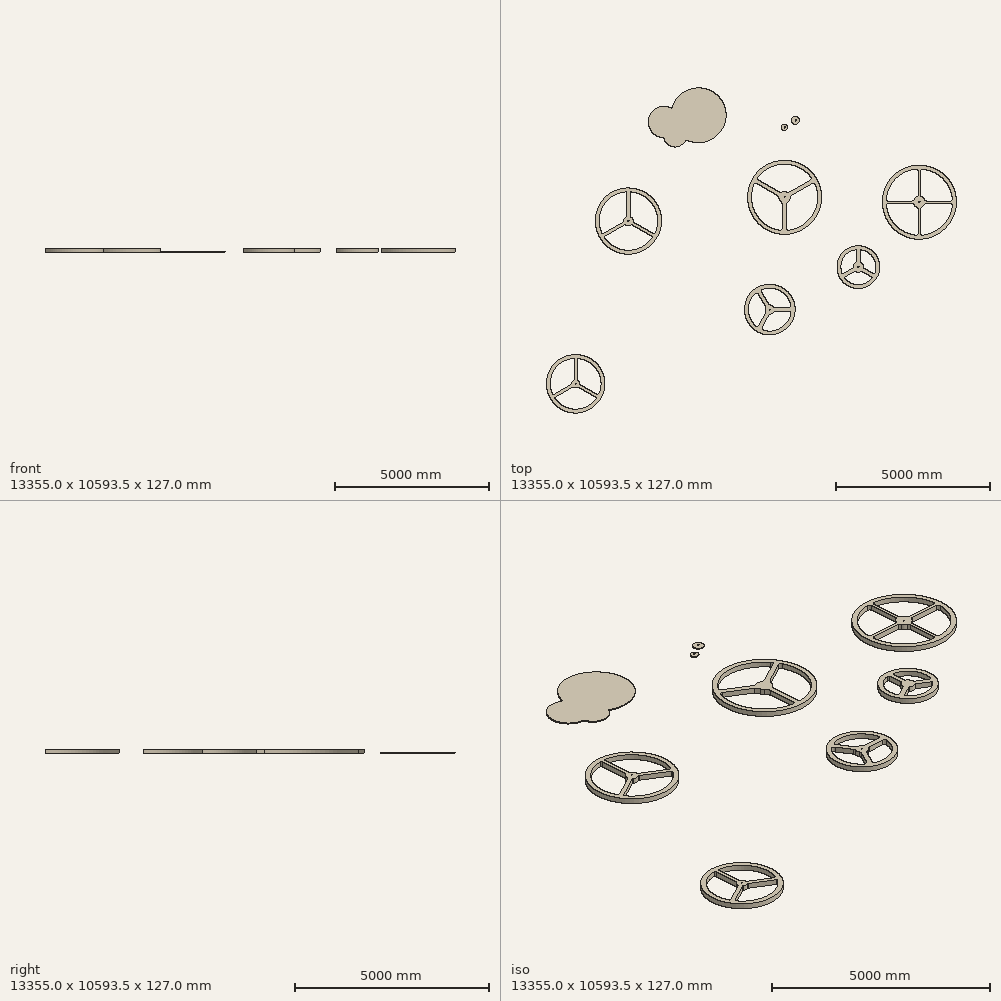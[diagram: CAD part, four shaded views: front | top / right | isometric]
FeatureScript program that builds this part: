
annotation { "Feature Type Name" : "Feature", "Feature Type Description" : "" }
export const myFeature = defineFeature(function(context is Context, id is Id, definition is map)
    precondition{}
    {
        {
            var Q0;
            Q0=qCreatedBy(makeId("Top.planeOp"),FACE);
            var sketch = newSketch(context, id + "F0", { "sketchPlane" : qUnion([Q0])});
            skCircle(sketch, "E0", {"center": v(0, 0) * mm, "radius": 1206.5 * mm});
            skCircle(sketch, "E1", {"center": v(2359.54, 1934.63) * mm, "radius": 304.8 * mm});
            skLineSegment(sketch, "E2", {"start": v(-904.95, 449.15) * mm, "end": v(-250.23, 71.15) * mm});
            skLineSegment(sketch, "E3", {"start": v(-841.45, 559.13) * mm, "end": v(-186.73, 181.13) * mm});
            skArc(sketch, "E4", {"start": v(134.94, -1071.29) * mm, "mid": v(935.1, -539.88) * mm, "end": v(995.23, 418.79) * mm});
            skLineSegment(sketch, "E5.MirrorCS", {"start": v(-63.5, -1008.28) * mm, "end": v(-63.5, -252.28) * mm});
            skLineSegment(sketch, "E6.MirrorCS", {"start": v(63.5, -1008.28) * mm, "end": v(63.5, -252.28) * mm});
            skPoint(sketch, "E7.orphan", {"position": v(-28.72, -56.74) * mm});
            skLineSegment(sketch, "E8.trimOffspring", {"start": v(-935.1, 539.88) * mm, "end": v(-935.78, 540.27) * mm});
            skPoint(sketch, "E9.newPointB", {"position": v(-63.5, -1080.55) * mm});
            skArc(sketch, "E9.filletArc", {"start": v(-134.94, -1071.29) * mm, "mid": v(-85, -1055.9) * mm, "end": v(-63.5, -1008.28) * mm});
            skPoint(sketch, "E10.newPointA", {"position": v(63.5, -1080.55) * mm});
            skArc(sketch, "E10.filletArc", {"start": v(63.5, -1008.28) * mm, "mid": v(85, -1055.9) * mm, "end": v(134.94, -1071.29) * mm});
            skArc(sketch, "E11.MirrorCS", {"start": v(860.3, 652.5) * mm, "mid": v(871.94, 601.56) * mm, "end": v(841.45, 559.13) * mm});
            skArc(sketch, "E12.MirrorCS", {"start": v(904.95, 449.15) * mm, "mid": v(956.94, 454.34) * mm, "end": v(995.23, 418.79) * mm});
            skArc(sketch, "E13.MirrorCS", {"start": v(-860.3, 652.5) * mm, "mid": v(-871.94, 601.56) * mm, "end": v(-841.45, 559.13) * mm});
            skArc(sketch, "E14.MirrorCS", {"start": v(-904.95, 449.15) * mm, "mid": v(-956.94, 454.34) * mm, "end": v(-995.23, 418.79) * mm});
            skArc(sketch, "E15.trimOffspring", {"start": v(-995.23, 418.79) * mm, "mid": v(-935.1, -539.88) * mm, "end": v(-134.94, -1071.29) * mm});
            skLineSegment(sketch, "E16.trimOffspring", {"start": v(841.45, 559.13) * mm, "end": v(186.73, 181.13) * mm});
            skArc(sketch, "E17.trimOffspring", {"start": v(860.3, 652.5) * mm, "mid": v(0, 1079.75) * mm, "end": v(-860.3, 652.5) * mm});
            skLineSegment(sketch, "E18.trimOffspring", {"start": v(904.95, 449.15) * mm, "end": v(250.23, 71.15) * mm});
            skPoint(sketch, "E19.MirrorCS.start.orphan", {"position": v(967.53, 485.28) * mm});
            skPoint(sketch, "E20.MirrorCS.start.orphan", {"position": v(904.03, 595.27) * mm});
            skPoint(sketch, "E21.visualSharp", {"position": v(0, 73.32) * mm});
            skCircle(sketch, "E22", {"center": v(2511.94, 1934.63) * mm, "radius": 80.55 * mm});
            skCircle(sketch, "E23.MirrorC", {"center": v(2359.54, 2087.03) * mm, "radius": 80.55 * mm});
            skCircle(sketch, "E24.MirrorC", {"center": v(2359.54, 1782.23) * mm, "radius": 80.55 * mm});
            skCircle(sketch, "E25.MirrorC", {"center": v(2207.14, 1934.63) * mm, "radius": 80.55 * mm});
            skLineSegment(sketch, "E26.trimOffspring", {"start": v(2431.4, 1934.63) * mm, "end": v(2592.49, 1934.63) * mm});
            skPoint(sketch, "E27.orphan", {"position": v(2664.34, 1934.63) * mm});
            skArc(sketch, "E28", {"start": v(-188.4, -28.18) * mm, "mid": v(-168.26, -89.32) * mm, "end": v(-128.9, -140.26) * mm});
            skLineSegment(sketch, "E29", {"start": v(0, 0) * mm, "end": v(-16.5, 9.53) * mm});
            skArc(sketch, "E30", {"start": v(-186.73, 181.13) * mm, "mid": v(-121.81, 169.22) * mm, "end": v(-57.02, 181.77) * mm});
            skArc(sketch, "E31.MirrorCS", {"start": v(-250.23, 71.15) * mm, "mid": v(-207.46, 20.88) * mm, "end": v(-185.92, -41.5) * mm});
            skLineSegment(sketch, "E32", {"start": v(0, 0) * mm, "end": v(0, -19.05) * mm});
            skArc(sketch, "E33.MirrorCS", {"start": v(186.73, 181.13) * mm, "mid": v(121.81, 169.22) * mm, "end": v(57.02, 181.77) * mm});
            skArc(sketch, "E34.MirrorCS", {"start": v(250.23, 71.15) * mm, "mid": v(207.46, 20.88) * mm, "end": v(185.92, -41.5) * mm});
            skArc(sketch, "E35.MirrorCS", {"start": v(63.5, -252.28) * mm, "mid": v(85.64, -190.1) * mm, "end": v(128.9, -140.26) * mm});
            skArc(sketch, "E36.MirrorCS", {"start": v(-63.5, -252.28) * mm, "mid": v(-85.64, -190.1) * mm, "end": v(-128.9, -140.26) * mm});
            skArc(sketch, "E37.trimOffspring", {"start": v(69.8, 177.25) * mm, "mid": v(0, 190.5) * mm, "end": v(-69.8, 177.25) * mm});
            skArc(sketch, "E38.trimOffspring", {"start": v(118.6, -149.07) * mm, "mid": v(161.49, -101.06) * mm, "end": v(185.92, -41.5) * mm});
            skCircle(sketch, "E39", {"center": v(1177.08, 2703.2) * mm, "radius": 304.8 * mm});
            skCircle(sketch, "E40", {"center": v(1329.48, 2703.2) * mm, "radius": 80.55 * mm});
            skCircle(sketch, "E41.MirrorC", {"center": v(1177.08, 2855.6) * mm, "radius": 80.55 * mm});
            skCircle(sketch, "E42.MirrorC", {"center": v(1177.08, 2550.8) * mm, "radius": 80.55 * mm});
            skCircle(sketch, "E43.MirrorC", {"center": v(1024.68, 2703.2) * mm, "radius": 80.55 * mm});
            skLineSegment(sketch, "E44.trimOffspring", {"start": v(1248.93, 2703.2) * mm, "end": v(1410.03, 2703.2) * mm});
            skPoint(sketch, "E45.orphan", {"position": v(1481.88, 2703.2) * mm});
            skCircle(sketch, "E46", {"center": v(1177.08, 2703.2) * mm, "radius": 21.59 * mm});
            skLineSegment(sketch, "E47", {"start": v(1177.08, 2703.2) * mm, "end": v(1177.08, 2724.8) * mm});
            skLineSegment(sketch, "E48", {"start": v(1177.08, 2703.2) * mm, "end": v(1192.35, 2718.47) * mm});
            skLineSegment(sketch, "E49", {"start": v(1177.08, 2855.6) * mm, "end": v(1177.08, 2936.15) * mm});
            skLineSegment(sketch, "E50", {"start": v(1177.08, 2703.2) * mm, "end": v(1198.67, 2703.2) * mm});
            skLineSegment(sketch, "E51", {"start": v(1296.75, 2822.88) * mm, "end": v(1367.02, 2893.15) * mm});
            skCircle(sketch, "E52", {"center": v(1331.89, 2858.01) * mm, "radius": 49.69 * mm});
            skCircle(sketch, "E53.MirrorC", {"center": v(1022.27, 2858.01) * mm, "radius": 49.69 * mm});
            skCircle(sketch, "E54.MirrorC", {"center": v(1022.27, 2548.4) * mm, "radius": 49.69 * mm});
            skCircle(sketch, "E55.MirrorC", {"center": v(1331.89, 2548.4) * mm, "radius": 49.69 * mm});
            skLineSegment(sketch, "E56.trimOffspring", {"start": v(1177.08, 2775.06) * mm, "end": v(1177.08, 2855.6) * mm});
            skCircle(sketch, "E57", {"center": v(4388.83, -157.21) * mm, "radius": 1206.5 * mm});
            skCircle(sketch, "E58", {"center": v(4388.83, -157.21) * mm, "radius": 22.86 * mm});
            skArc(sketch, "E59", {"start": v(4465.03, -331.81) * mm, "mid": v(4523.53, -291.92) * mm, "end": v(4563.43, -233.41) * mm});
            skArc(sketch, "E60", {"start": v(4496.78, -1231.3) * mm, "mid": v(5152.15, -920.54) * mm, "end": v(5462.92, -265.16) * mm});
            skLineSegment(sketch, "E61", {"start": v(4388.83, -157.21) * mm, "end": v(4388.83, -180.07) * mm});
            skLineSegment(sketch, "E62", {"start": v(4388.83, -157.21) * mm, "end": v(4405, -173.38) * mm});
            skLineSegment(sketch, "E63.bottom", {"start": v(6717.68, -259.59) * mm, "end": v(7126.18, -259.59) * mm});
            skLineSegment(sketch, "E63.top", {"start": v(6781.18, -1038.61) * mm, "end": v(7126.18, -1038.61) * mm});
            skLineSegment(sketch, "E63.left", {"start": v(6717.68, -259.59) * mm, "end": v(6717.68, -975.11) * mm});
            skLineSegment(sketch, "E63.right", {"start": v(7189.68, -323.09) * mm, "end": v(7189.68, -975.11) * mm});
            skPoint(sketch, "E64.visualSharp", {"position": v(7189.68, -259.59) * mm});
            skArc(sketch, "E64.filletArc", {"start": v(7189.68, -323.09) * mm, "mid": v(7171.08, -278.19) * mm, "end": v(7126.18, -259.59) * mm});
            skPoint(sketch, "E65.visualSharp", {"position": v(6717.68, -1038.61) * mm});
            skArc(sketch, "E65.filletArc", {"start": v(6717.68, -975.11) * mm, "mid": v(6736.28, -1020.02) * mm, "end": v(6781.18, -1038.61) * mm});
            skPoint(sketch, "E66.visualSharp", {"position": v(4426.93, -343.87) * mm});
            skArc(sketch, "E66.filletArc", {"start": v(4465.03, -331.81) * mm, "mid": v(4437.3, -355.23) * mm, "end": v(4426.93, -390) * mm});
            skPoint(sketch, "E67.visualSharp", {"position": v(4350.73, -343.87) * mm});
            skArc(sketch, "E67.filletArc", {"start": v(4350.73, -390) * mm, "mid": v(4340.36, -355.23) * mm, "end": v(4312.63, -331.81) * mm});
            skLineSegment(sketch, "E68", {"start": v(4350.73, -1168.12) * mm, "end": v(4350.73, -390) * mm});
            skLineSegment(sketch, "E69", {"start": v(4426.93, -390) * mm, "end": v(4426.93, -1168.12) * mm});
            skPoint(sketch, "E70.visualSharp", {"position": v(7189.68, -1038.61) * mm});
            skArc(sketch, "E70.filletArc", {"start": v(7126.18, -1038.61) * mm, "mid": v(7171.08, -1020.02) * mm, "end": v(7189.68, -975.11) * mm});
            skPoint(sketch, "E71.visualSharp", {"position": v(4426.93, -1236.04) * mm});
            skArc(sketch, "E71.filletArc", {"start": v(4426.93, -1168.12) * mm, "mid": v(4447.83, -1215.21) * mm, "end": v(4496.78, -1231.3) * mm});
            skPoint(sketch, "E72.visualSharp", {"position": v(4350.73, -1236.04) * mm});
            skArc(sketch, "E72.filletArc", {"start": v(4280.88, -1231.3) * mm, "mid": v(4329.83, -1215.21) * mm, "end": v(4350.73, -1168.12) * mm});
            skArc(sketch, "E73.MirrorCS", {"start": v(4563.43, -233.41) * mm, "mid": v(4586.85, -205.69) * mm, "end": v(4621.63, -195.31) * mm});
            skArc(sketch, "E74.MirrorCS", {"start": v(4621.63, -119.11) * mm, "mid": v(4586.85, -108.74) * mm, "end": v(4563.43, -81.01) * mm});
            skLineSegment(sketch, "E75.MirrorCS", {"start": v(5399.74, -119.11) * mm, "end": v(4621.63, -119.11) * mm});
            skLineSegment(sketch, "E76.MirrorCS", {"start": v(4621.63, -195.31) * mm, "end": v(5399.74, -195.31) * mm});
            skArc(sketch, "E77.MirrorCS", {"start": v(5399.74, -195.31) * mm, "mid": v(5446.83, -216.22) * mm, "end": v(5462.92, -265.16) * mm});
            skArc(sketch, "E78.MirrorCS", {"start": v(5462.92, -49.26) * mm, "mid": v(5446.83, -98.21) * mm, "end": v(5399.74, -119.11) * mm});
            skArc(sketch, "E79.MirrorCS", {"start": v(4156.04, -119.11) * mm, "mid": v(4190.82, -108.74) * mm, "end": v(4214.23, -81.01) * mm});
            skLineSegment(sketch, "E80.MirrorCS", {"start": v(3377.92, -119.11) * mm, "end": v(4156.04, -119.11) * mm});
            skLineSegment(sketch, "E81.MirrorCS", {"start": v(4156.04, -195.31) * mm, "end": v(3377.92, -195.31) * mm});
            skArc(sketch, "E82.MirrorCS", {"start": v(4214.23, -233.41) * mm, "mid": v(4190.82, -205.69) * mm, "end": v(4156.04, -195.31) * mm});
            skArc(sketch, "E83.MirrorCS", {"start": v(3377.92, -195.31) * mm, "mid": v(3330.83, -216.22) * mm, "end": v(3314.74, -265.16) * mm});
            skArc(sketch, "E84.MirrorCS", {"start": v(3314.74, -49.26) * mm, "mid": v(3330.83, -98.21) * mm, "end": v(3377.92, -119.11) * mm});
            skLineSegment(sketch, "E85.MirrorCS", {"start": v(4426.93, 75.58) * mm, "end": v(4426.93, 853.7) * mm});
            skLineSegment(sketch, "E86.MirrorCS", {"start": v(4350.73, 853.7) * mm, "end": v(4350.73, 75.58) * mm});
            skArc(sketch, "E87.MirrorCS", {"start": v(4350.73, 75.58) * mm, "mid": v(4340.36, 40.8) * mm, "end": v(4312.63, 17.38) * mm});
            skPoint(sketch, "E88.MirrorP", {"position": v(4426.93, 29.44) * mm});
            skArc(sketch, "E89.MirrorCS", {"start": v(4465.03, 17.38) * mm, "mid": v(4437.3, 40.8) * mm, "end": v(4426.93, 75.58) * mm});
            skArc(sketch, "E90.MirrorCS", {"start": v(4426.93, 853.7) * mm, "mid": v(4447.83, 900.79) * mm, "end": v(4496.78, 916.87) * mm});
            skArc(sketch, "E91.MirrorCS", {"start": v(4280.88, 916.87) * mm, "mid": v(4329.83, 900.79) * mm, "end": v(4350.73, 853.7) * mm});
            skArc(sketch, "E92.trimOffspring", {"start": v(3314.74, -265.16) * mm, "mid": v(3625.5, -920.54) * mm, "end": v(4280.88, -1231.3) * mm});
            skArc(sketch, "E93.trimOffspring", {"start": v(4214.23, -233.41) * mm, "mid": v(4254.13, -291.92) * mm, "end": v(4312.63, -331.81) * mm});
            skArc(sketch, "E94.trimOffspring", {"start": v(4312.63, 17.38) * mm, "mid": v(4254.13, -22.51) * mm, "end": v(4214.23, -81.01) * mm});
            skArc(sketch, "E95.trimOffspring", {"start": v(4563.43, -81.01) * mm, "mid": v(4523.53, -22.51) * mm, "end": v(4465.03, 17.38) * mm});
            skLineSegment(sketch, "E96.trimOffspring", {"start": v(4523.53, -291.92) * mm, "end": v(5152.15, -920.54) * mm});
            skArc(sketch, "E97.trimOffspring", {"start": v(5462.92, -49.26) * mm, "mid": v(5152.15, 606.1) * mm, "end": v(4496.78, 916.87) * mm});
            skArc(sketch, "E98.trimOffspring", {"start": v(4280.88, 916.87) * mm, "mid": v(3625.5, 606.1) * mm, "end": v(3314.74, -49.26) * mm});
            skCircle(sketch, "E99", {"center": v(2359.54, 1934.63) * mm, "radius": 20.32 * mm});
            skCircle(sketch, "E100", {"center": v(0, 2278.33) * mm, "radius": 22.99 * mm});
            skCircle(sketch, "E101", {"center": v(0, 0) * mm, "radius": 19.05 * mm});
            skCircle(sketch, "E102", {"center": v(2402.2, -2273.62) * mm, "radius": 698.5 * mm});
            skArc(sketch, "E103", {"start": v(2309.16, -1709.75) * mm, "mid": v(1907.27, -1987.87) * mm, "end": v(1867.35, -2475) * mm});
            skArc(sketch, "E104", {"start": v(2325.15, -2127.6) * mm, "mid": v(2259.22, -2191.07) * mm, "end": v(2237.22, -2279.9) * mm});
            skLineSegment(sketch, "E105", {"start": v(2338.7, -1769.9) * mm, "end": v(2338.7, -2105.14) * mm});
            skLineSegment(sketch, "E106", {"start": v(2465.7, -1769.9) * mm, "end": v(2465.7, -2121.22) * mm});
            skLineSegment(sketch, "E107", {"start": v(2465.7, -2105.14) * mm, "end": v(2465.7, -1734.8) * mm});
            skLineSegment(sketch, "E108", {"start": v(2338.7, -1769.9) * mm, "end": v(2338.7, -1734.8) * mm});
            skLineSegment(sketch, "E109", {"start": v(1999.56, -1360.97) * mm, "end": v(1999.56, -1432.2) * mm});
            skLineSegment(sketch, "E110", {"start": v(2024.96, -1457.6) * mm, "end": v(2120.48, -1457.6) * mm});
            skPoint(sketch, "E111.visualSharp", {"position": v(1999.56, -1457.6) * mm});
            skArc(sketch, "E111.filletArc", {"start": v(1999.56, -1432.2) * mm, "mid": v(2007, -1450.16) * mm, "end": v(2024.96, -1457.6) * mm});
            skPoint(sketch, "E112.visualSharp", {"position": v(2338.7, -1705.66) * mm});
            skArc(sketch, "E112.filletArc", {"start": v(2338.7, -1734.8) * mm, "mid": v(2329.73, -1715.44) * mm, "end": v(2309.16, -1709.75) * mm});
            skPoint(sketch, "E113.visualSharp", {"position": v(2465.7, -1705.66) * mm});
            skArc(sketch, "E113.filletArc", {"start": v(2495.23, -1709.75) * mm, "mid": v(2474.66, -1715.44) * mm, "end": v(2465.7, -1734.8) * mm});
            skPoint(sketch, "E114.visualSharp", {"position": v(2338.7, -2121.22) * mm});
            skArc(sketch, "E114.filletArc", {"start": v(2325.15, -2127.6) * mm, "mid": v(2335.05, -2118.26) * mm, "end": v(2338.7, -2105.14) * mm});
            skPoint(sketch, "E115.visualSharp", {"position": v(2465.7, -2121.22) * mm});
            skArc(sketch, "E115.filletArc", {"start": v(2465.7, -2105.14) * mm, "mid": v(2469.35, -2118.26) * mm, "end": v(2479.25, -2127.6) * mm});
            skLineSegment(sketch, "E116.MirrorCS", {"start": v(1934.21, -2470.5) * mm, "end": v(2224.54, -2302.87) * mm});
            skLineSegment(sketch, "E117.MirrorCS", {"start": v(2288.04, -2412.86) * mm, "end": v(1967.32, -2598.02) * mm});
            skArc(sketch, "E118.MirrorCS", {"start": v(2237.22, -2279.9) * mm, "mid": v(2234.07, -2293.16) * mm, "end": v(2224.54, -2302.87) * mm});
            skArc(sketch, "E119.MirrorCS", {"start": v(2288.04, -2412.86) * mm, "mid": v(2301.22, -2409.46) * mm, "end": v(2314.26, -2413.36) * mm});
            skArc(sketch, "E120.MirrorCS", {"start": v(1903.82, -2488.04) * mm, "mid": v(1882.57, -2489.96) * mm, "end": v(1867.35, -2475) * mm});
            skArc(sketch, "E121.MirrorCS", {"start": v(1960.38, -2636.13) * mm, "mid": v(1955.03, -2615.47) * mm, "end": v(1967.32, -2598.02) * mm});
            skLineSegment(sketch, "E122.MirrorCS", {"start": v(1934.21, -2470.5) * mm, "end": v(1903.82, -2488.04) * mm});
            skLineSegment(sketch, "E123.MirrorCS", {"start": v(2870.19, -2470.5) * mm, "end": v(2579.86, -2302.87) * mm});
            skLineSegment(sketch, "E124.MirrorCS", {"start": v(2516.36, -2412.86) * mm, "end": v(2837.08, -2598.02) * mm});
            skArc(sketch, "E125.MirrorCS", {"start": v(2516.36, -2412.86) * mm, "mid": v(2503.18, -2409.46) * mm, "end": v(2490.13, -2413.36) * mm});
            skArc(sketch, "E126.MirrorCS", {"start": v(2479.25, -2127.6) * mm, "mid": v(2545.18, -2191.07) * mm, "end": v(2567.18, -2279.9) * mm});
            skArc(sketch, "E127.MirrorCS", {"start": v(2567.18, -2279.9) * mm, "mid": v(2570.33, -2293.16) * mm, "end": v(2579.86, -2302.87) * mm});
            skArc(sketch, "E128.MirrorCS", {"start": v(2900.58, -2488.04) * mm, "mid": v(2921.83, -2489.96) * mm, "end": v(2937.05, -2475) * mm});
            skArc(sketch, "E129.MirrorCS", {"start": v(2844.01, -2636.13) * mm, "mid": v(2849.37, -2615.47) * mm, "end": v(2837.08, -2598.02) * mm});
            skLineSegment(sketch, "E130.MirrorCS", {"start": v(2870.19, -2470.5) * mm, "end": v(2900.58, -2488.04) * mm});
            skArc(sketch, "E131.trimOffspring", {"start": v(1960.38, -2636.13) * mm, "mid": v(2402.2, -2845.12) * mm, "end": v(2844.01, -2636.13) * mm});
            skArc(sketch, "E132.trimOffspring", {"start": v(2937.05, -2475) * mm, "mid": v(2897.13, -1987.87) * mm, "end": v(2495.23, -1709.75) * mm});
            skArc(sketch, "E133.trimOffspring", {"start": v(2567.18, -2279.9) * mm, "mid": v(2545.18, -2191.07) * mm, "end": v(2479.25, -2127.6) * mm});
            skArc(sketch, "E134.trimOffspring", {"start": v(2314.26, -2413.36) * mm, "mid": v(2402.2, -2438.72) * mm, "end": v(2490.13, -2413.36) * mm});
            skArc(sketch, "E135.trimOffspring", {"start": v(2490.13, -2413.36) * mm, "mid": v(2402.2, -2438.72) * mm, "end": v(2314.26, -2413.36) * mm});
            skArc(sketch, "E136.trimOffspring", {"start": v(2237.22, -2279.9) * mm, "mid": v(2259.22, -2191.07) * mm, "end": v(2325.15, -2127.6) * mm});
            skCircle(sketch, "E137", {"center": v(2402.2, -2273.62) * mm, "radius": 19.05 * mm});
            skCircle(sketch, "E138", {"center": v(-482.79, -3656.25) * mm, "radius": 825.5 * mm});
            skArc(sketch, "E139", {"start": v(-623.21, -3597.03) * mm, "mid": v(-635.16, -3659.18) * mm, "end": v(-620.83, -3720.83) * mm});
            skLineSegment(sketch, "E140", {"start": v(-518.6, -3473.95) * mm, "end": v(-749.8, -3090.72) * mm});
            skLineSegment(sketch, "E141", {"start": v(-749.8, -3090.72) * mm, "end": v(-518.6, -3473.95) * mm});
            skPoint(sketch, "E142.visualSharp", {"position": v(-787.74, -3027.83) * mm});
            skArc(sketch, "E142.filletArc", {"start": v(-716.7, -2998.08) * mm, "mid": v(-755.23, -3036.54) * mm, "end": v(-749.8, -3090.72) * mm});
            skPoint(sketch, "E143.visualSharp", {"position": v(-499.98, -3504.82) * mm});
            skArc(sketch, "E143.filletArc", {"start": v(-518.6, -3473.95) * mm, "mid": v(-497.8, -3495.05) * mm, "end": v(-469.7, -3504.42) * mm});
            skArc(sketch, "E144.MirrorCS", {"start": v(-955.93, -3142.4) * mm, "mid": v(-903.94, -3126.26) * mm, "end": v(-858.55, -3156.32) * mm});
            skLineSegment(sketch, "E145.MirrorCS", {"start": v(-627.35, -3539.55) * mm, "end": v(-858.55, -3156.32) * mm});
            skArc(sketch, "E146.MirrorCS", {"start": v(-627.35, -3539.55) * mm, "mid": v(-618.38, -3567.8) * mm, "end": v(-623.21, -3597.03) * mm});
            skPoint(sketch, "E147.orphan", {"position": v(-896.48, -3093.44) * mm});
            skArc(sketch, "E148.trimOffspring", {"start": v(-955.93, -3142.4) * mm, "mid": v(-1181.16, -3669.68) * mm, "end": v(-935.83, -4187.9) * mm});
            skPoint(sketch, "E149.orphan", {"position": v(-507.14, -3492.96) * mm});
            skPoint(sketch, "E150.orphan", {"position": v(-615.88, -3558.56) * mm});
            skLineSegment(sketch, "E151.MirrorCS", {"start": v(-307, -3716.38) * mm, "end": v(140.49, -3707.78) * mm});
            skLineSegment(sketch, "E152.MirrorCS", {"start": v(138.05, -3580.8) * mm, "end": v(-309.44, -3589.4) * mm});
            skArc(sketch, "E153.MirrorCS", {"start": v(-309.44, -3589.4) * mm, "mid": v(-338.38, -3583.05) * mm, "end": v(-361.29, -3564.25) * mm});
            skArc(sketch, "E154.MirrorCS", {"start": v(-307, -3716.38) * mm, "mid": v(-335.68, -3723.85) * mm, "end": v(-357.84, -3743.51) * mm});
            skArc(sketch, "E155.MirrorCS", {"start": v(204.16, -3782.77) * mm, "mid": v(190.12, -3730.17) * mm, "end": v(140.49, -3707.78) * mm});
            skArc(sketch, "E156.MirrorCS", {"start": v(198.79, -3503.42) * mm, "mid": v(186.78, -3556.52) * mm, "end": v(138.05, -3580.8) * mm});
            skLineSegment(sketch, "E157.MirrorCS", {"start": v(-622.76, -3778.42) * mm, "end": v(-839.05, -4170.26) * mm});
            skLineSegment(sketch, "E158.MirrorCS", {"start": v(-727.86, -4231.63) * mm, "end": v(-511.57, -3839.8) * mm});
            skArc(sketch, "E159.MirrorCS", {"start": v(-691.22, -4322.93) * mm, "mid": v(-731.2, -4285.98) * mm, "end": v(-727.86, -4231.63) * mm});
            skArc(sketch, "E160.MirrorCS", {"start": v(-935.83, -4187.9) * mm, "mid": v(-883.25, -4202.04) * mm, "end": v(-839.05, -4170.26) * mm});
            skArc(sketch, "E161.MirrorCS", {"start": v(-511.57, -3839.8) * mm, "mid": v(-491.6, -3817.9) * mm, "end": v(-463.86, -3807.47) * mm});
            skArc(sketch, "E162.MirrorCS", {"start": v(-622.76, -3778.42) * mm, "mid": v(-614.88, -3749.85) * mm, "end": v(-620.83, -3720.83) * mm});
            skArc(sketch, "E163.trimOffspring", {"start": v(-463.86, -3807.47) * mm, "mid": v(-404.06, -3786.74) * mm, "end": v(-357.84, -3743.51) * mm});
            skArc(sketch, "E164.trimOffspring", {"start": v(-361.29, -3564.25) * mm, "mid": v(-409.14, -3522.83) * mm, "end": v(-469.7, -3504.42) * mm});
            skArc(sketch, "E165.trimOffspring", {"start": v(198.79, -3503.42) * mm, "mid": v(-145.23, -3044.73) * mm, "end": v(-716.7, -2998.08) * mm});
            skArc(sketch, "E166.trimOffspring", {"start": v(-691.22, -4322.93) * mm, "mid": v(-121.97, -4254.34) * mm, "end": v(204.16, -3782.77) * mm});
            skCircle(sketch, "E167", {"center": v(-482.79, -3656.25) * mm, "radius": 19.05 * mm});
            skCircle(sketch, "E168", {"center": v(-5086.57, -770.76) * mm, "radius": 1079.5 * mm});
            skArc(sketch, "E169", {"start": v(-5164.86, 178.51) * mm, "mid": v(-5911.46, -294.51) * mm, "end": v(-5947.81, -1177.6) * mm});
            skArc(sketch, "E170", {"start": v(-5151.88, -633.07) * mm, "mid": v(-5218.55, -694.56) * mm, "end": v(-5238.47, -783.05) * mm});
            skCircle(sketch, "E171", {"center": v(0, 2278.33) * mm, "radius": 101.6 * mm});
            skCircle(sketch, "E172", {"center": v(355.23, 2506.68) * mm, "radius": 22.99 * mm});
            skCircle(sketch, "E173", {"center": v(355.23, 2506.68) * mm, "radius": 134.38 * mm});
            skCircle(sketch, "E174", {"center": v(-6807.19, -6073.12) * mm, "radius": 952.5 * mm});
            skArc(sketch, "E175", {"start": v(-6885.8, -5251.38) * mm, "mid": v(-7522.1, -5660.37) * mm, "end": v(-7558.15, -6415.91) * mm});
            skLineSegment(sketch, "E176", {"start": v(-5137.37, 153.2) * mm, "end": v(-5137.37, -610.12) * mm});
            skLineSegment(sketch, "E177", {"start": v(-5035.77, 153.2) * mm, "end": v(-5035.77, -610.12) * mm});
            skLineSegment(sketch, "E178.bottom", {"start": v(-3589.34, -293.86) * mm, "end": v(-3407.23, -293.86) * mm});
            skLineSegment(sketch, "E178.top", {"start": v(-3570.29, -575.44) * mm, "end": v(-3419.93, -575.44) * mm});
            skLineSegment(sketch, "E178.left", {"start": v(-3595.69, -300.21) * mm, "end": v(-3595.69, -550.04) * mm});
            skLineSegment(sketch, "E178.right", {"start": v(-3394.53, -306.56) * mm, "end": v(-3394.53, -550.04) * mm});
            skPoint(sketch, "E179.visualSharp", {"position": v(-3595.69, -293.86) * mm});
            skArc(sketch, "E179.filletArc", {"start": v(-3589.34, -293.86) * mm, "mid": v(-3593.83, -295.72) * mm, "end": v(-3595.69, -300.21) * mm});
            skPoint(sketch, "E180.visualSharp", {"position": v(-3394.53, -293.86) * mm});
            skArc(sketch, "E180.filletArc", {"start": v(-3394.53, -306.56) * mm, "mid": v(-3398.25, -297.58) * mm, "end": v(-3407.23, -293.86) * mm});
            skPoint(sketch, "E181.visualSharp", {"position": v(-3394.53, -575.44) * mm});
            skArc(sketch, "E181.filletArc", {"start": v(-3419.93, -575.44) * mm, "mid": v(-3401.97, -568) * mm, "end": v(-3394.53, -550.04) * mm});
            skPoint(sketch, "E182.visualSharp", {"position": v(-3595.69, -575.44) * mm});
            skArc(sketch, "E182.filletArc", {"start": v(-3595.69, -550.04) * mm, "mid": v(-3588.25, -568) * mm, "end": v(-3570.29, -575.44) * mm});
            skPoint(sketch, "E183.visualSharp", {"position": v(-5035.77, 180.38) * mm});
            skArc(sketch, "E183.filletArc", {"start": v(-5008.28, 178.51) * mm, "mid": v(-5027.58, 171.88) * mm, "end": v(-5035.77, 153.2) * mm});
            skPoint(sketch, "E184.visualSharp", {"position": v(-5137.37, 180.38) * mm});
            skArc(sketch, "E184.filletArc", {"start": v(-5137.37, 153.2) * mm, "mid": v(-5145.56, 171.88) * mm, "end": v(-5164.86, 178.51) * mm});
            skLineSegment(sketch, "E185.bottom", {"start": v(-3521.85, 165.33) * mm, "end": v(-3268.73, 165.33) * mm});
            skLineSegment(sketch, "E185.top", {"start": v(-3496.45, -14.92) * mm, "end": v(-3268.73, -14.92) * mm});
            skLineSegment(sketch, "E185.left", {"start": v(-3521.85, 165.33) * mm, "end": v(-3521.85, 10.48) * mm});
            skLineSegment(sketch, "E185.right", {"start": v(-3268.73, 165.33) * mm, "end": v(-3268.73, -14.92) * mm});
            skPoint(sketch, "E186.visualSharp", {"position": v(-3521.85, -14.92) * mm});
            skArc(sketch, "E186.filletArc", {"start": v(-3521.85, 10.48) * mm, "mid": v(-3514.41, -7.48) * mm, "end": v(-3496.45, -14.92) * mm});
            skPoint(sketch, "E187.visualSharp", {"position": v(-5035.77, -627.08) * mm});
            skArc(sketch, "E187.filletArc", {"start": v(-5035.77, -610.12) * mm, "mid": v(-5031.84, -623.7) * mm, "end": v(-5021.26, -633.07) * mm});
            skPoint(sketch, "E188.visualSharp", {"position": v(-5137.37, -627.08) * mm});
            skArc(sketch, "E188.filletArc", {"start": v(-5151.88, -633.07) * mm, "mid": v(-5141.3, -623.7) * mm, "end": v(-5137.37, -610.12) * mm});
            skLineSegment(sketch, "E189.MirrorCS", {"start": v(-5861.35, -1276.74) * mm, "end": v(-5200.3, -895.08) * mm});
            skLineSegment(sketch, "E190.MirrorCS", {"start": v(-5912.15, -1188.75) * mm, "end": v(-5251.1, -807.1) * mm});
            skArc(sketch, "E191.MirrorCS", {"start": v(-5238.47, -783.05) * mm, "mid": v(-5241.3, -796.9) * mm, "end": v(-5251.1, -807.1) * mm});
            skArc(sketch, "E192.MirrorCS", {"start": v(-5200.3, -895.08) * mm, "mid": v(-5186.57, -891.7) * mm, "end": v(-5173.16, -896.17) * mm});
            skArc(sketch, "E193.MirrorCS", {"start": v(-5912.15, -1188.75) * mm, "mid": v(-5932.42, -1191) * mm, "end": v(-5947.81, -1177.6) * mm});
            skArc(sketch, "E194.MirrorCS", {"start": v(-5869.52, -1313.2) * mm, "mid": v(-5873.43, -1293.18) * mm, "end": v(-5861.35, -1276.74) * mm});
            skLineSegment(sketch, "E195.MirrorCS", {"start": v(-4261, -1188.75) * mm, "end": v(-4922.05, -807.1) * mm});
            skLineSegment(sketch, "E196.MirrorCS", {"start": v(-4311.8, -1276.74) * mm, "end": v(-4972.85, -895.08) * mm});
            skArc(sketch, "E197.MirrorCS", {"start": v(-4999.98, -896.17) * mm, "mid": v(-4986.57, -891.7) * mm, "end": v(-4972.85, -895.08) * mm});
            skArc(sketch, "E198.MirrorCS", {"start": v(-4922.05, -807.1) * mm, "mid": v(-4931.84, -796.9) * mm, "end": v(-4934.67, -783.05) * mm});
            skArc(sketch, "E199.MirrorCS", {"start": v(-4311.8, -1276.74) * mm, "mid": v(-4299.71, -1293.18) * mm, "end": v(-4303.62, -1313.2) * mm});
            skArc(sketch, "E200.MirrorCS", {"start": v(-4225.33, -1177.6) * mm, "mid": v(-4240.72, -1191) * mm, "end": v(-4261, -1188.75) * mm});
            skArc(sketch, "E201.trimOffspring", {"start": v(-5869.52, -1313.2) * mm, "mid": v(-5086.57, -1723.26) * mm, "end": v(-4303.62, -1313.2) * mm});
            skArc(sketch, "E202.trimOffspring", {"start": v(-4225.33, -1177.6) * mm, "mid": v(-4261.68, -294.51) * mm, "end": v(-5008.28, 178.51) * mm});
            skArc(sketch, "E203.trimOffspring", {"start": v(-4934.67, -783.05) * mm, "mid": v(-4954.59, -694.56) * mm, "end": v(-5021.26, -633.07) * mm});
            skArc(sketch, "E204.trimOffspring", {"start": v(-5173.16, -896.17) * mm, "mid": v(-5086.57, -923.16) * mm, "end": v(-4999.98, -896.17) * mm});
            skArc(sketch, "E205", {"start": v(-6870.69, -5963.14) * mm, "mid": v(-6917.18, -6009.62) * mm, "end": v(-6934.19, -6073.12) * mm});
            skLineSegment(sketch, "E206", {"start": v(-6756.39, -5276.66) * mm, "end": v(-6756.39, -5941.14) * mm});
            skLineSegment(sketch, "E207", {"start": v(-6857.99, -5276.66) * mm, "end": v(-6857.99, -5941.14) * mm});
            skLineSegment(sketch, "E208.bottom", {"start": v(-8632.4, -5662.84) * mm, "end": v(-8538.47, -5662.84) * mm});
            skLineSegment(sketch, "E208.top", {"start": v(-8632.4, -5862.78) * mm, "end": v(-8513.07, -5862.78) * mm});
            skLineSegment(sketch, "E208.left", {"start": v(-8632.4, -5662.84) * mm, "end": v(-8632.4, -5862.78) * mm});
            skLineSegment(sketch, "E208.right", {"start": v(-8513.07, -5688.24) * mm, "end": v(-8513.07, -5862.78) * mm});
            skPoint(sketch, "E209.visualSharp", {"position": v(-8513.07, -5662.84) * mm});
            skArc(sketch, "E209.filletArc", {"start": v(-8513.07, -5688.24) * mm, "mid": v(-8520.51, -5670.28) * mm, "end": v(-8538.47, -5662.84) * mm});
            skPoint(sketch, "E210.visualSharp", {"position": v(-6756.39, -5249.19) * mm});
            skArc(sketch, "E210.filletArc", {"start": v(-6728.57, -5251.38) * mm, "mid": v(-6748.07, -5257.86) * mm, "end": v(-6756.39, -5276.66) * mm});
            skPoint(sketch, "E211.visualSharp", {"position": v(-6857.99, -5249.19) * mm});
            skArc(sketch, "E211.filletArc", {"start": v(-6857.99, -5276.66) * mm, "mid": v(-6866.3, -5257.86) * mm, "end": v(-6885.8, -5251.38) * mm});
            skPoint(sketch, "E212.visualSharp", {"position": v(-6756.39, -5956.73) * mm});
            skArc(sketch, "E212.filletArc", {"start": v(-6756.39, -5941.14) * mm, "mid": v(-6752.99, -5953.84) * mm, "end": v(-6743.69, -5963.14) * mm});
            skPoint(sketch, "E213.visualSharp", {"position": v(-6857.99, -5956.73) * mm});
            skArc(sketch, "E213.filletArc", {"start": v(-6870.69, -5963.14) * mm, "mid": v(-6861.4, -5953.84) * mm, "end": v(-6857.99, -5941.14) * mm});
            skArc(sketch, "E214.MirrorCS", {"start": v(-6743.69, -6183.1) * mm, "mid": v(-6730.99, -6179.7) * mm, "end": v(-6718.29, -6183.1) * mm});
            skLineSegment(sketch, "E215.MirrorCS", {"start": v(-6142.83, -6515.35) * mm, "end": v(-6718.29, -6183.1) * mm});
            skArc(sketch, "E216.MirrorCS", {"start": v(-6667.49, -6095.12) * mm, "mid": v(-6676.79, -6085.82) * mm, "end": v(-6680.19, -6073.12) * mm});
            skLineSegment(sketch, "E217.MirrorCS", {"start": v(-6092.03, -6427.36) * mm, "end": v(-6667.49, -6095.12) * mm});
            skArc(sketch, "E218.MirrorCS", {"start": v(-6142.83, -6515.35) * mm, "mid": v(-6130.71, -6531.95) * mm, "end": v(-6134.84, -6552.08) * mm});
            skArc(sketch, "E219.MirrorCS", {"start": v(-6056.23, -6415.91) * mm, "mid": v(-6071.6, -6429.56) * mm, "end": v(-6092.03, -6427.36) * mm});
            skLineSegment(sketch, "E220.MirrorCS", {"start": v(-7471.55, -6515.35) * mm, "end": v(-6896.09, -6183.1) * mm});
            skLineSegment(sketch, "E221.MirrorCS", {"start": v(-7522.35, -6427.36) * mm, "end": v(-6946.89, -6095.12) * mm});
            skArc(sketch, "E222.MirrorCS", {"start": v(-6934.19, -6073.12) * mm, "mid": v(-6937.6, -6085.82) * mm, "end": v(-6946.89, -6095.12) * mm});
            skArc(sketch, "E223.MirrorCS", {"start": v(-6896.09, -6183.1) * mm, "mid": v(-6883.39, -6179.7) * mm, "end": v(-6870.69, -6183.1) * mm});
            skArc(sketch, "E224.MirrorCS", {"start": v(-7522.35, -6427.36) * mm, "mid": v(-7542.78, -6429.56) * mm, "end": v(-7558.15, -6415.91) * mm});
            skArc(sketch, "E225.MirrorCS", {"start": v(-7479.53, -6552.08) * mm, "mid": v(-7483.67, -6531.95) * mm, "end": v(-7471.55, -6515.35) * mm});
            skArc(sketch, "E226.trimOffspring", {"start": v(-6870.69, -6183.1) * mm, "mid": v(-6807.19, -6200.12) * mm, "end": v(-6743.69, -6183.1) * mm});
            skArc(sketch, "E227.trimOffspring", {"start": v(-6680.19, -6073.12) * mm, "mid": v(-6697.2, -6009.62) * mm, "end": v(-6743.69, -5963.14) * mm});
            skArc(sketch, "E228.trimOffspring", {"start": v(-7479.53, -6552.08) * mm, "mid": v(-6807.19, -6898.62) * mm, "end": v(-6134.84, -6552.08) * mm});
            skArc(sketch, "E229.trimOffspring", {"start": v(-6056.23, -6415.91) * mm, "mid": v(-6092.29, -5660.37) * mm, "end": v(-6728.57, -5251.38) * mm});
            skCircle(sketch, "E230", {"center": v(-5086.57, -770.76) * mm, "radius": 19.05 * mm});
            skCircle(sketch, "E231", {"center": v(-6807.19, -6073.12) * mm, "radius": 19.05 * mm});
            skCircle(sketch, "E232", {"center": v(-3925.77, 2452.66) * mm, "radius": 512.9 * mm});
            skCircle(sketch, "E233", {"center": v(-2801.77, 2672.52) * mm, "radius": 895.37 * mm});
            skCircle(sketch, "E234", {"center": v(-3563.37, 2027.51) * mm, "radius": 387.76 * mm});
            skSolve(sketch);
        }
        {
            var Q0;
            Q0=makeQuery(id+"F0.imprint","IMPRINT",FACE,{"disambiguationData":[TD([[makeQuery(id+"F0.imprint","IMPRINT",EDGE,{"derivedFrom":sQuery(id+"F0.wireOp",EDGE,"E0")}),1.0]])]});
            var Q1;
            Q1=makeQuery(id+"F0.imprint","IMPRINT",FACE,{"disambiguationData":[TD([[makeQuery(id+"F0.imprint","IMPRINT",EDGE,{"derivedFrom":sQuery(id+"F0.wireOp",EDGE,"E102")}),1.0]])]});
            var Q2;
            Q2=makeQuery(id+"F0.imprint","IMPRINT",FACE,{"disambiguationData":[TD([[makeQuery(id+"F0.imprint","IMPRINT",EDGE,{"derivedFrom":sQuery(id+"F0.wireOp",EDGE,"E57")}),1.0]])]});
            extrude(context, id + "F1", {"entities" : qUnion([Q0, Q1, Q2]), "depth" : 127 * mm, "offsetDistance" : 25.4 * mm});
        }
        {
            var Q0;
            Q0=makeQuery(id+"F0.imprint","IMPRINT",FACE,{"disambiguationData":[TD([[makeQuery(id+"F0.imprint","IMPRINT",EDGE,{"derivedFrom":sQuery(id+"F0.wireOp",EDGE,"E138")}),1.0]])]});
            extrude(context, id + "F2", {"entities" : qUnion([Q0]), "depth" : 127 * mm, "offsetDistance" : 25.4 * mm});
        }
        {
            var Q0;
            Q0=makeQuery(id+"F0.imprint","IMPRINT",FACE,{"disambiguationData":[TD([[makeQuery(id+"F0.imprint","IMPRINT",EDGE,{"derivedFrom":sQuery(id+"F0.wireOp",EDGE,"E100")}),-1.0]])]});
            var Q1;
            Q1=makeQuery(id+"F0.imprint","IMPRINT",FACE,{"disambiguationData":[TD([[makeQuery(id+"F0.imprint","IMPRINT",EDGE,{"derivedFrom":sQuery(id+"F0.wireOp",EDGE,"E172")}),-1.0]])]});
            extrude(context, id + "F3", {"entities" : qUnion([Q0, Q1]), "depth" : 25.4 * mm, "offsetDistance" : 25.4 * mm});
        }
        {
            var Q0;
            Q0=makeQuery(id+"F0.imprint","IMPRINT",FACE,{"disambiguationData":[TD([[makeQuery(id+"F0.imprint","IMPRINT",EDGE,{"derivedFrom":sQuery(id+"F0.wireOp",EDGE,"E174")}),1.0]])]});
            var Q1;
            Q1=makeQuery(id+"F0.imprint","IMPRINT",FACE,{"disambiguationData":[TD([[makeQuery(id+"F0.imprint","IMPRINT",EDGE,{"derivedFrom":sQuery(id+"F0.wireOp",EDGE,"E168")}),1.0]])]});
            extrude(context, id + "F4", {"entities" : qUnion([Q0, Q1]), "depth" : 127 * mm, "offsetDistance" : 25.4 * mm});
        }
        {
            var Q0;
            {var subQ0=sQuery(id+"F0.wireOp",EDGE,"E234");var subQ1=sQuery(id+"F0.wireOp",EDGE,"E232");var subQ2=makeQuery(id+"F0.imprint","INTERSECT",VERTEX,{"disambiguationData":[OD(0.0)],"derivedFrom":[subQ1,subQ0]});Q0=makeQuery(id+"F0.imprint","IMPRINT",FACE,{"disambiguationData":[TD([[makeQuery(id+"F0.imprint","IMPRINT",EDGE,{"disambiguationData":[TD([[subQ2,-1.0]])],"derivedFrom":subQ1}),-1.0]])]});}
            var Q1;
            {var subQ0=sQuery(id+"F0.wireOp",EDGE,"E234");var subQ1=sQuery(id+"F0.wireOp",EDGE,"E232");var subQ2=makeQuery(id+"F0.imprint","INTERSECT",VERTEX,{"disambiguationData":[OD(0.0)],"derivedFrom":[subQ1,subQ0]});Q1=makeQuery(id+"F0.imprint","IMPRINT",FACE,{"disambiguationData":[TD([[makeQuery(id+"F0.imprint","IMPRINT",EDGE,{"disambiguationData":[TD([[subQ2,-1.0]])],"derivedFrom":subQ1}),1.0]])]});}
            var Q2;
            {var subQ0=sQuery(id+"F0.wireOp",EDGE,"E234");var subQ1=sQuery(id+"F0.wireOp",EDGE,"E232");var subQ2=makeQuery(id+"F0.imprint","INTERSECT",VERTEX,{"disambiguationData":[OD(0.0)],"derivedFrom":[subQ1,subQ0]});Q2=makeQuery(id+"F0.imprint","IMPRINT",FACE,{"disambiguationData":[TD([[makeQuery(id+"F0.imprint","IMPRINT",EDGE,{"disambiguationData":[TD([[subQ2,1.0]])],"derivedFrom":subQ1}),1.0]])]});}
            var Q3;
            {var subQ0=sQuery(id+"F0.wireOp",EDGE,"E233");var subQ1=sQuery(id+"F0.wireOp",EDGE,"E232");var subQ2=makeQuery(id+"F0.imprint","INTERSECT",VERTEX,{"disambiguationData":[OD(0.0)],"derivedFrom":[subQ1,subQ0]});Q3=makeQuery(id+"F0.imprint","IMPRINT",FACE,{"disambiguationData":[TD([[makeQuery(id+"F0.imprint","IMPRINT",EDGE,{"disambiguationData":[TD([[subQ2,1.0]])],"derivedFrom":subQ1}),1.0]])]});}
            var Q4;
            {var subQ0=sQuery(id+"F0.wireOp",EDGE,"E233");var subQ1=sQuery(id+"F0.wireOp",EDGE,"E232");var subQ2=makeQuery(id+"F0.imprint","INTERSECT",VERTEX,{"disambiguationData":[OD(1.0)],"derivedFrom":[subQ1,subQ0]});Q4=makeQuery(id+"F0.imprint","IMPRINT",FACE,{"disambiguationData":[TD([[makeQuery(id+"F0.imprint","IMPRINT",EDGE,{"disambiguationData":[TD([[subQ2,-1.0]])],"derivedFrom":subQ1}),1.0]])]});}
            var Q5;
            {var subQ0=sQuery(id+"F0.wireOp",EDGE,"E233");var subQ1=sQuery(id+"F0.wireOp",EDGE,"E232");var subQ2=makeQuery(id+"F0.imprint","INTERSECT",VERTEX,{"disambiguationData":[OD(1.0)],"derivedFrom":[subQ1,subQ0]});Q5=makeQuery(id+"F0.imprint","IMPRINT",FACE,{"disambiguationData":[TD([[makeQuery(id+"F0.imprint","IMPRINT",EDGE,{"disambiguationData":[TD([[subQ2,-1.0]])],"derivedFrom":subQ1}),-1.0]])]});}
            var Q6;
            {var subQ0=sQuery(id+"F0.wireOp",EDGE,"E233");var subQ1=sQuery(id+"F0.wireOp",EDGE,"E232");var subQ2=makeQuery(id+"F0.imprint","INTERSECT",VERTEX,{"disambiguationData":[OD(0.0)],"derivedFrom":[subQ1,subQ0]});Q6=makeQuery(id+"F0.imprint","IMPRINT",FACE,{"disambiguationData":[TD([[makeQuery(id+"F0.imprint","IMPRINT",EDGE,{"disambiguationData":[TD([[subQ2,1.0]])],"derivedFrom":subQ1}),-1.0]])]});}
            extrude(context, id + "F5", {"entities" : qUnion([Q0, Q1, Q2, Q3, Q4, Q5, Q6]), "depth" : 25.4 * mm, "offsetDistance" : 25.4 * mm});
        }
    });
